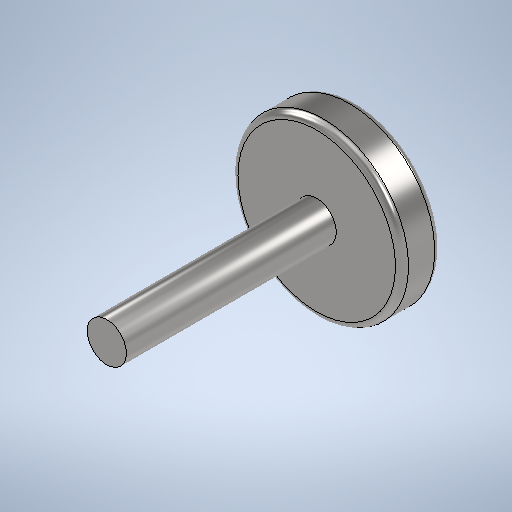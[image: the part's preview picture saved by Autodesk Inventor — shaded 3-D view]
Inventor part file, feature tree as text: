
AUTODESK INVENTOR PART (.ipt)
format: ipt  version: 2025 (Build 290162010, 162A)  size: 297,984 bytes
history: native  units: mm
features: extrude x3, sketch x3, fillet x1
ambient origin geometry x8: Origin, YZ Plane, XZ Plane, XY Plane, X Axis, Y Axis, Z Axis, Center Point
bodies: Volumenkörper1 (feature_tree)
feature tree (7):
  extrude  "Extrusion1"  Depth=6.0mm TaperAngle=0.0deg
  extrude  "Extrusion2"  Depth=32.0mm TaperAngle=0.0deg
  extrude  "Extrusion3"  Depth=9.5mm
  fillet  "Rundung1"  Radius=13.5mm
  sketch  "Skizze1"  dims[d0=26.0mm d1=6.0mm d2=0.0mm]
  sketch  "Skizze2"  dims[d3=6.0mm d4=32.0mm d5=0.0mm]
  sketch  "Skizze3"  dims[d6=3.0mm d7=9.5mm d8=13.5mm d9=0.0mm d10=1.0mm]
